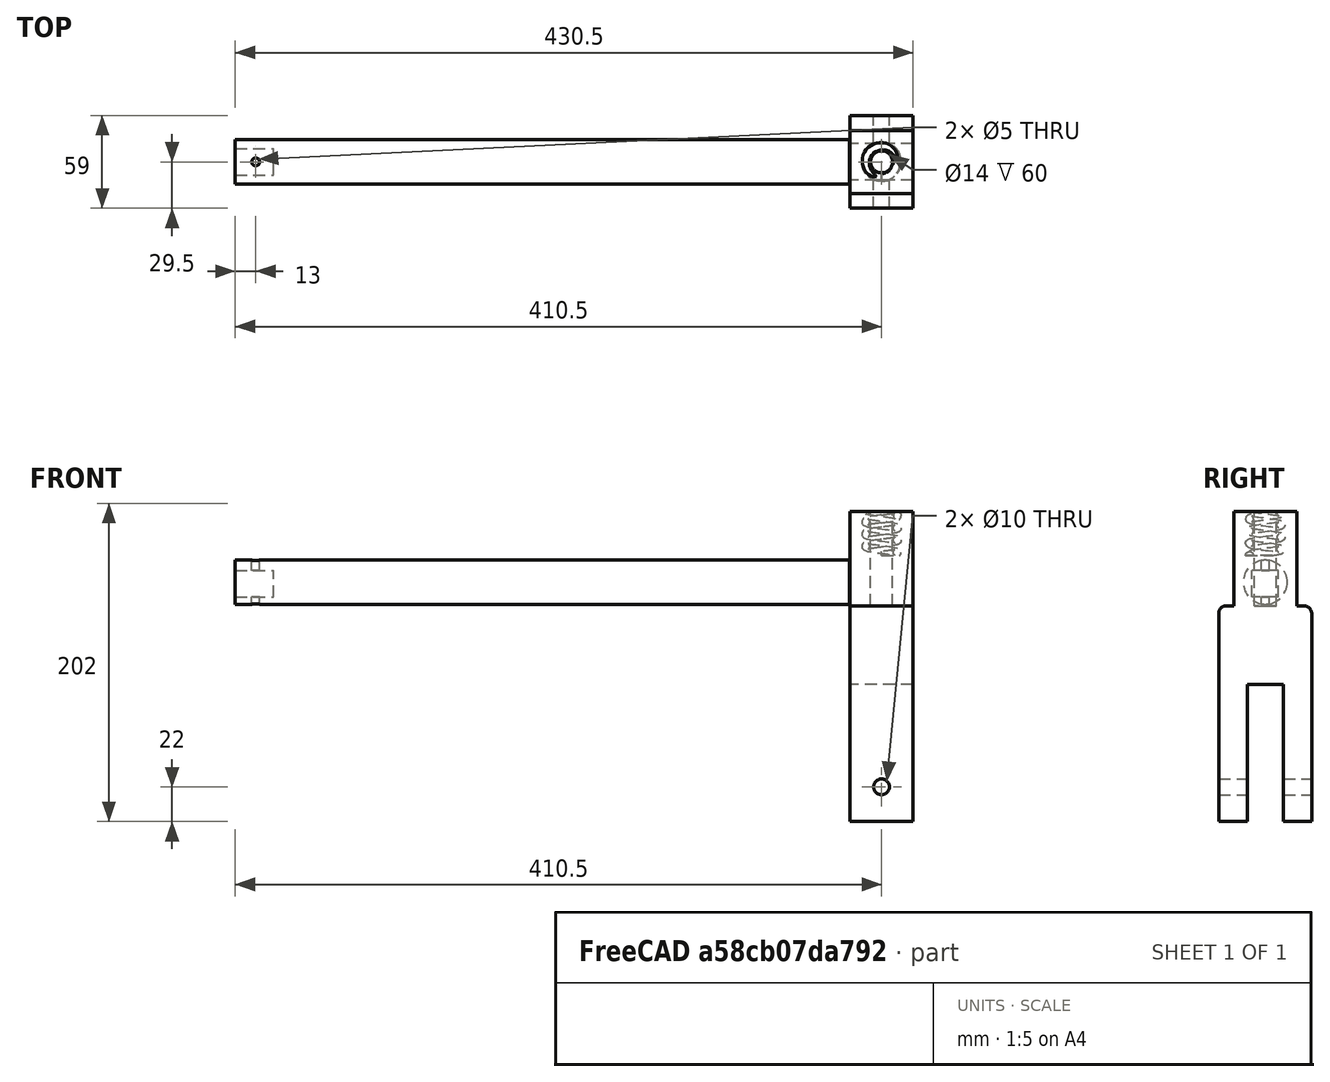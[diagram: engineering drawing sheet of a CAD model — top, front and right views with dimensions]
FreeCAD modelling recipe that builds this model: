
FCSTD DOCUMENT  (FreeCAD 0.16R6704 (Git))
Label: Object 5
License: All rights reserved
LicenseURL: http://en.wikipedia.org/wiki/All_rights_reserved
objects: Part::Cut×8, Part::Box×6, Part::Cylinder×4, Part::Sweep×1, Part::MultiFuse×1, Part::Fillet×1
note: 21 computed .brp shape members not serialized (recipe doc carries the construction recipe); baked Part::Feature solids carry a one-line shape summary decoded from their .brp

FEATURE [Part::Cylinder] Cylinder189  label="Cilindro106"
  Angle = 360
  Height = 390
  Placement = pos=(-0.5,0,0) rot=(0,1,0;1.5708rad)
  Radius = 14
FEATURE [Part::Box] Box118  label="Cubo080"
  Height = 60
  Length = 40
  Placement = pos=(400,-20,-15) rot=(0,0,1;0rad)
  Width = 40
FEATURE [Part::Box] Box119  label="Cubo081"
  Height = 137
  Length = 59
  Placement = pos=(0,-5,0) rot=(0,0,1;0rad)
  Width = 40
FEATURE [Part::Box] Box120  label="Cubo082"
  Height = 87
  Length = 23
  Placement = pos=(18,-5,0) rot=(0,0,1;0rad)
  Width = 40
FEATURE [Part::Cut] Cut237
  Base = -> Box119
  Tool = -> Box120
FEATURE [Part::Cylinder] Cylinder190  label="Cilindro107"
  Angle = 360
  Height = 59
  Placement = pos=(0,15,22) rot=(0,1,0;1.5708rad)
  Radius = 5
FEATURE [Part::Cut] Cut238
  Base = -> Cut237
  Placement = pos=(435,-29.5,-152) rot=(0,0,1;1.5708rad)
  Tool = -> Cylinder190
FEATURE [Part::Cylinder] Cylinder191  label="Cilindro108"
  Angle = 360
  Height = 60
  Placement = pos=(12.5,0,-17) rot=(0,0,1;0rad)
  Radius = 2.5
FEATURE [Part::Cut] Cut239
  Base = -> Cylinder189
  Placement = pos=(10,0,0) rot=(0,0,1;0rad)
  Tool = -> Cylinder191
FEATURE [Part::Cylinder] Cylinder192  label="qwer004"
  Angle = 360
  Height = 74
  Placement = pos=(420,0,-29) rot=(0,0,1;0rad)
  Radius = 7
FEATURE [Part::Cut] Cut240
  Base = -> Box118
  Tool = -> Cylinder192
FEATURE [Part::Sweep] Sweep010
  Frenet = true
  Placement = pos=(4,-76,0) rot=(0,0,-1;1.5708rad)
  Solid = true
  Transition = 1
FEATURE [Part::Box] Box121  label="Cubo083"
  Height = 6
  Length = 27
  Placement = pos=(0,-89,-6) rot=(0,0,1;0rad)
  Width = 25
FEATURE [Part::Cut] Cut241
  Base = -> Sweep010
  Tool = -> Box121
FEATURE [Part::Box] Box122  label="Cubo084"
  Height = 29
  Length = 32
  Placement = pos=(-9,-89,105) rot=(0,0,1;0rad)
  Width = 27
FEATURE [Part::Cut] Cut242  label="EL AMORTIGUADOR009"
  Base = -> Cut241
  Placement = pos=(416,76,17) rot=(0,0,1;0rad)
  Tool = -> Box122
FEATURE [Part::Cut] Cut243
  Base = -> Cut240
  Tool = -> Cut242
FEATURE [Part::MultiFuse] Fusion058
  Placement = pos=(-450,460,0) rot=(0,0,1;0rad)
  Shapes = -> [Cut239,Cut243,Cut238]
FEATURE [Part::Box] Box134  label="Cubo096"
  Height = 17
  Length = 27
  Placement = pos=(-443,451.5,-9.5) rot=(0,0,1;0rad)
  Width = 17
FEATURE [Part::Cut] Cut315
  Base = -> Fusion058
  Tool = -> Box134
FEATURE [Part::Fillet] Fillet
  Base = -> Cut315
  Edges = 2 edges r=4.9: [Edge18,Edge22]
